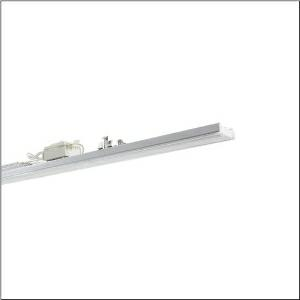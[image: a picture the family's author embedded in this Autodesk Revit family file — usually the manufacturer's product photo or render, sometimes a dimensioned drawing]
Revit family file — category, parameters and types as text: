
# Revit family: licross_r__11_recessed_ho_51tl1wdn4exm_4d1c
name_source: partatom
category: Lighting Fixtures
units: mm (PartAtom-declared; Revit-internal decimal feet)

## family parameters
Cut with Voids When Loaded = No
Host = Face
Light Source = No
Part Type = Normal
Room Calculation Point = No
Round Connector Dimension = Use Diameter
Shared = No

## types (1)
- --- (1 x LED, 14170 lm, 76.8 W, 4000K)
    Apparent Load = 77 VA
    CIE Flux Codes = 73 94 99 100 100
    Color Rendering = 80
    Color Temperature = 4000K
    Default Elevation = 1800 mm
    Description = Licross® 11 Recessed HO, luminaire insert, of sheet steel, coil coated, white, length: 1.500mm, width: 66mm, height: 67mm, LED rated luminous flux: 14.170lm, light colour: 840, control gear: DALI 2, with plug, 5-pole, with phase selection, mains connection: 220..240V, AC, 50/60Hz, rated input power: 77W, internal wiring halogen-free, primary optical cover: cover, of PMMA, light emission: direct distribution, primary light characteristic: symmetric, protection rating (complete): IP40, insulation class (complete): insulation class I (protective earthing), certification: CE, ENEC, VDE, UKCA, protection symbol: D if used in an environment without relevant dust loads with corresponding accessories, impact resistance: IK06, permissible ambient temperature for indoor applications: -25..+30°C, corresponds to IFS (International Featured Standards) requirements for safety and quality in the food industry, reducing of maximum allowable ambient temperature of 5°C with ceiling mounting, LABS conformity tested according to VDMA 24364:2018-05, packaging unit: 1 piece
    Height = 58 mm
    Lamp = 1 x LED
    Lamp Light Flux = 14170 lm
    Lamp Power = 76.8 W
    Lamp count = 1
    Length = 1500 mm
    Luminous efficacy = 185 lm/W
    Manufacturer = Siteco
    ModVariant = No
    Model = 51TL1WDN4EXM
    Mounting Place = Ceiling
    Mounting Type = Pendant
    Number of Poles = 1
    OnlyDefault = Yes
    Power Factor = 1
    Product Name = Licross® 11 Recessed HO
    Product group = luminaire insert | ceiling pendant
    ProductGroupID = 902
    Protection Class = Protection class I
    Protection Degree = IP 40
    RLX_Detail_Level = 1
    RLX_Emergency_Light_Flux = 0 lm
    RLX_Emergency_Type = 0
    RLX_Emergency_Type_DB = No
    RlxData = <blob elided: 24609 chars, md5=4507934f>
    Socket = socket
    Standby Power = 0 W
    System Light Flux = 14170 lm
    System Power = 77 W
    Type Comments = factory setting: luminous flux: 100 % | dim-lin: 254 | 522 mA
    Type Image = l_1296930.jpg
    URL = http://relux.com
    VarID = @adj_080191
    Voltage = 0 V
    Weight = 0.00 kg
    Width = 66 mm

## geometry (parser evidence)
native form markers: Blend x4, Sweep x13
no freeform markers — native parametric forms only
